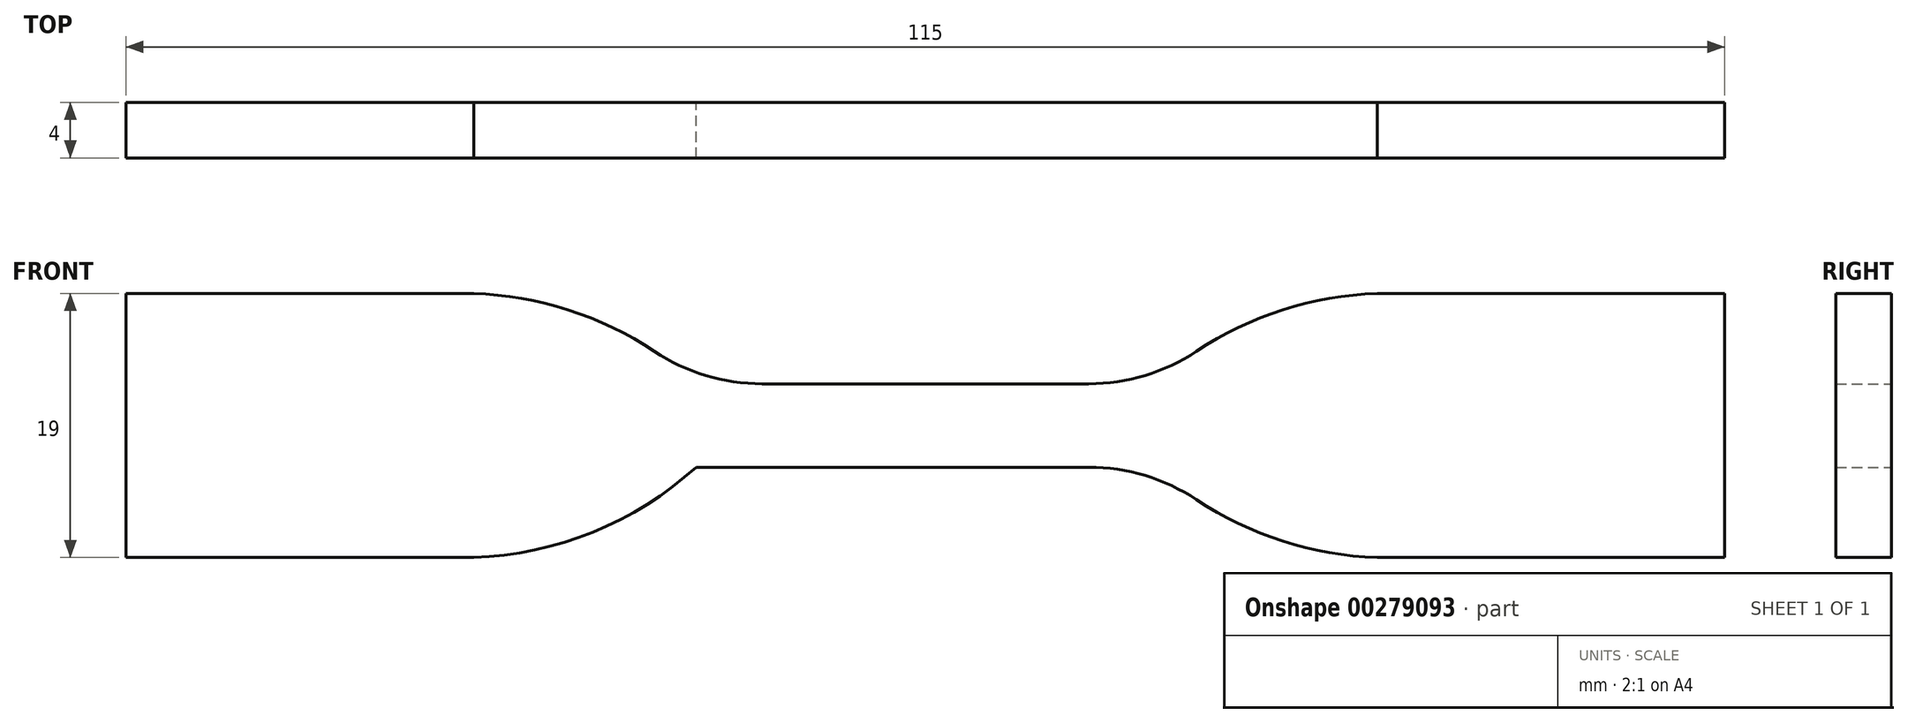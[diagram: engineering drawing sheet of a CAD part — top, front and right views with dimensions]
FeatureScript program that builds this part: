
annotation { "Feature Type Name" : "Feature", "Feature Type Description" : "" }
export const myFeature = defineFeature(function(context is Context, id is Id, definition is map)
    precondition{}
    {
        {
            var Q0;
            Q0=qCreatedBy(makeId("Front.planeOp"),FACE);
            var sketch = newSketch(context, id + "F0", { "sketchPlane" : qUnion([Q0])});
            skLineSegment(sketch, "E0", {"start": v(0, 3) * mm, "end": v(16.5, 3) * mm});
            skLineSegment(sketch, "E1", {"start": v(32.5, 9.5) * mm, "end": v(57.5, 9.5) * mm});
            skLineSegment(sketch, "E2", {"start": v(57.5, 9.5) * mm, "end": v(57.5, 0) * mm});
            skLineSegment(sketch, "E3.MirrorCS", {"start": v(32.5, -9.5) * mm, "end": v(57.5, -9.5) * mm});
            skLineSegment(sketch, "E4.MirrorCS", {"start": v(57.5, -9.5) * mm, "end": v(57.5, 0) * mm});
            skLineSegment(sketch, "E5.MirrorCS", {"start": v(0, -3) * mm, "end": v(16.5, -3) * mm});
            skLineSegment(sketch, "E6.MirrorCS", {"start": v(0, -3) * mm, "end": v(11.75, -3) * mm});
            skLineSegment(sketch, "E7.MirrorCS", {"start": v(0, 3) * mm, "end": v(11.75, 3) * mm});
            skLineSegment(sketch, "E8.MirrorCS", {"start": v(-32.5, -9.5) * mm, "end": v(-57.5, -9.5) * mm});
            skLineSegment(sketch, "E9.MirrorCS", {"start": v(-32.5, 9.5) * mm, "end": v(-57.5, 9.5) * mm});
            skLineSegment(sketch, "E10.MirrorCS", {"start": v(-57.5, 9.5) * mm, "end": v(-57.5, 0) * mm});
            skLineSegment(sketch, "E11.MirrorCS", {"start": v(0, 3) * mm, "end": v(-11.75, 3) * mm});
            skLineSegment(sketch, "E12.MirrorCS", {"start": v(-57.5, -9.5) * mm, "end": v(-57.5, 0) * mm});
            skLineSegment(sketch, "E13.MirrorCS", {"start": v(0, -3) * mm, "end": v(-16.5, -3) * mm});
            skLineSegment(sketch, "E14.MirrorCS", {"start": v(0, 3) * mm, "end": v(-16.5, 3) * mm});
            skLineSegment(sketch, "E15.MirrorCS", {"start": v(0, -3) * mm, "end": v(-11.75, -3) * mm});
            skArc(sketch, "E16.MirrorCS", {"start": v(-16.5, -3) * mm, "mid": v(-23.92, -7.68) * mm, "end": v(-32.5, -9.5) * mm});
            skArc(sketch, "E17.MirrorCS", {"start": v(-19.5, -5.34) * mm, "mid": v(-25.7, -8.32) * mm, "end": v(-32.5, -9.5) * mm});
            skArc(sketch, "E18.MirrorCS", {"start": v(-19.5, 5.34) * mm, "mid": v(-25.7, 8.32) * mm, "end": v(-32.5, 9.5) * mm});
            skArc(sketch, "E19.MirrorCS", {"start": v(19.5, -5.34) * mm, "mid": v(25.7, -8.32) * mm, "end": v(32.5, -9.5) * mm});
            skArc(sketch, "E20.MirrorCS", {"start": v(19.5, 5.34) * mm, "mid": v(25.7, 8.32) * mm, "end": v(32.5, 9.5) * mm});
            skPoint(sketch, "E21.visualSharp", {"position": v(-16.5, 3) * mm});
            skArc(sketch, "E21.filletArc", {"start": v(-19.5, 5.34) * mm, "mid": v(-15.8, 3.6) * mm, "end": v(-11.75, 3) * mm});
            skArc(sketch, "E22.filletArc", {"start": v(-11.75, -3) * mm, "mid": v(-15.8, -3.6) * mm, "end": v(-19.5, -5.34) * mm});
            skPoint(sketch, "E23.visualSharp", {"position": v(16.5, 3) * mm});
            skArc(sketch, "E23.filletArc", {"start": v(11.75, 3) * mm, "mid": v(15.8, 3.6) * mm, "end": v(19.5, 5.34) * mm});
            skPoint(sketch, "E24.visualSharp", {"position": v(16.5, -3) * mm});
            skArc(sketch, "E24.filletArc", {"start": v(19.5, -5.34) * mm, "mid": v(15.8, -3.6) * mm, "end": v(11.75, -3) * mm});
            skSolve(sketch);
        }
        {
            var Q0;
            Q0=makeQuery(id+"F0.imprint","IMPRINT",FACE,{"disambiguationData":[TD([[makeQuery(id+"F0.imprint","IMPRINT",EDGE,{"derivedFrom":sQuery(id+"F0.wireOp",EDGE,"E3.MirrorCS")}),1.0]])]});
            extrude(context, id + "F1", {"entities" : qUnion([Q0]), "endBound" : BoundingType.SYMMETRIC, "depth" : 4 * mm});
        }
    });
